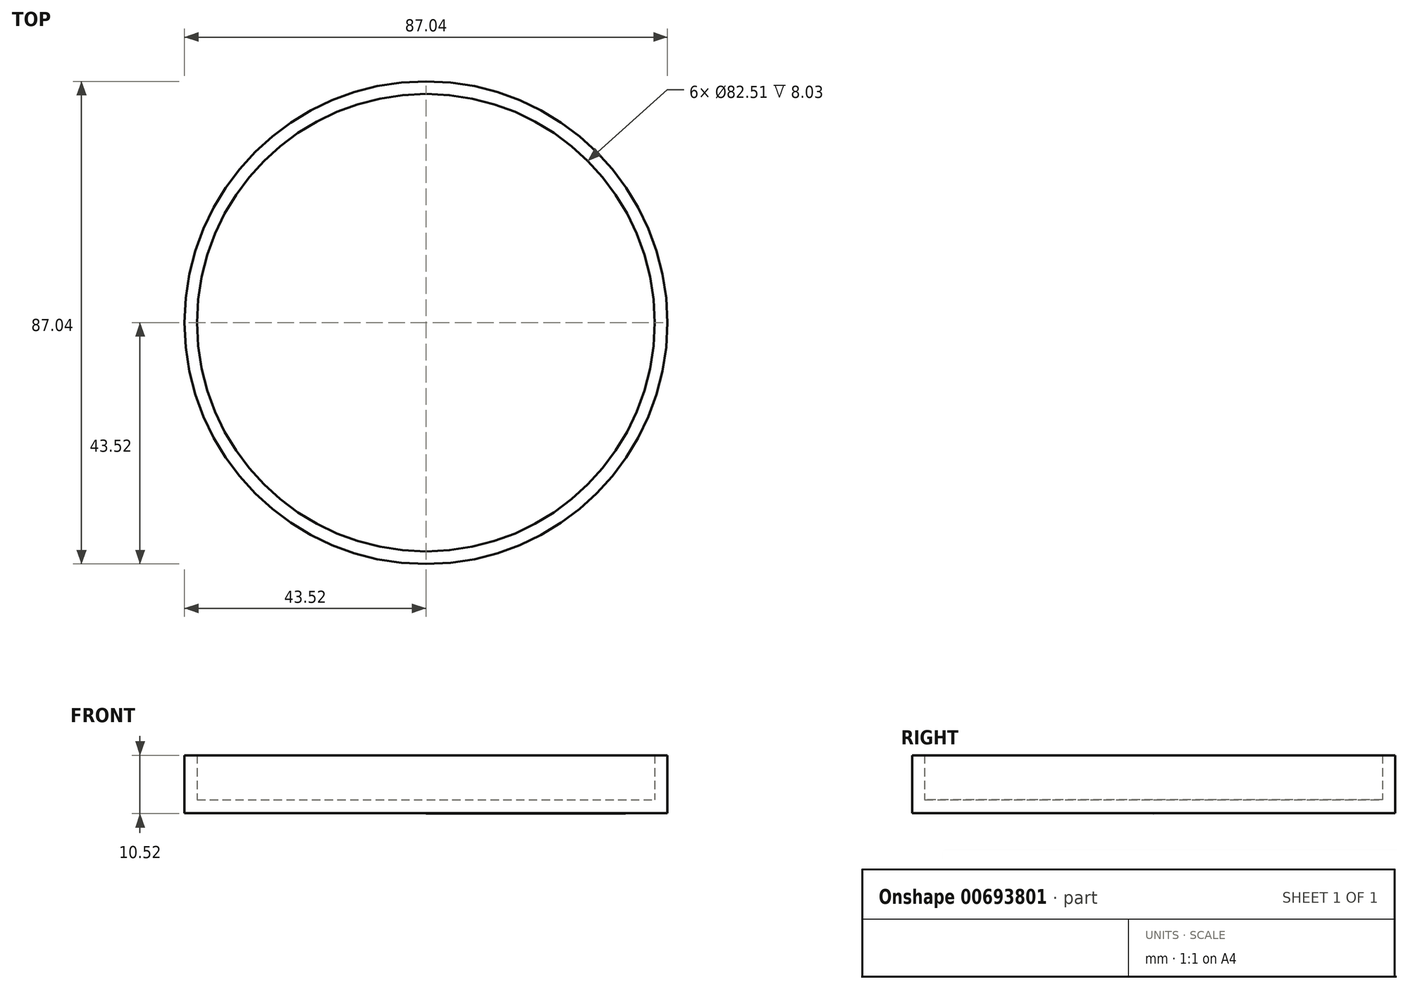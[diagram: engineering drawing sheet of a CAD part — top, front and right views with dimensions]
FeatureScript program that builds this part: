
annotation { "Feature Type Name" : "Feature", "Feature Type Description" : "" }
export const myFeature = defineFeature(function(context is Context, id is Id, definition is map)
    precondition{}
    {
        {
            var Q0;
            Q0=qCreatedBy(makeId("Front.planeOp"),FACE);
            var sketch = newSketch(context, id + "F0", { "sketchPlane" : qUnion([Q0])});
            skLineSegment(sketch, "E0", {"start": v(0, -1.42) * mm, "end": v(0, 1.07) * mm});
            skPoint(sketch, "E1.MirrorCS.end.orphan", {"position": v(0, 1.07) * mm});
            skPoint(sketch, "E2.MirrorCS.end.orphan", {"position": v(0, -1.42) * mm});
            skLineSegment(sketch, "E3", {"start": v(0, 1.07) * mm, "end": v(41.25, 1.07) * mm});
            skLineSegment(sketch, "E4", {"start": v(41.25, 1.07) * mm, "end": v(41.25, 9.1) * mm});
            skLineSegment(sketch, "E5", {"start": v(41.25, 9.1) * mm, "end": v(43.52, 9.1) * mm});
            skLineSegment(sketch, "E6", {"start": v(43.52, 9.1) * mm, "end": v(43.52, -1.35) * mm});
            skLineSegment(sketch, "E7", {"start": v(0, -1.42) * mm, "end": v(43.52, -1.35) * mm});
            skSolve(sketch);
        }
        {
            var Q0;
            Q0=makeQuery(id+"F0.imprint","IMPRINT",FACE,{"disambiguationData":[TD([[makeQuery(id+"F0.imprint","IMPRINT",EDGE,{"derivedFrom":sQuery(id+"F0.wireOp",EDGE,"E0")}),-1.0]])]});
            var Q1;
            Q1=sQuery(id+"F0.wireOp",EDGE,"E0");
            revolve(context, id + "F1", {"entities" : qUnion([Q0]), "axis" : qUnion([Q1]), "revolveType" : RevolveType.FULL});
        }
    });
